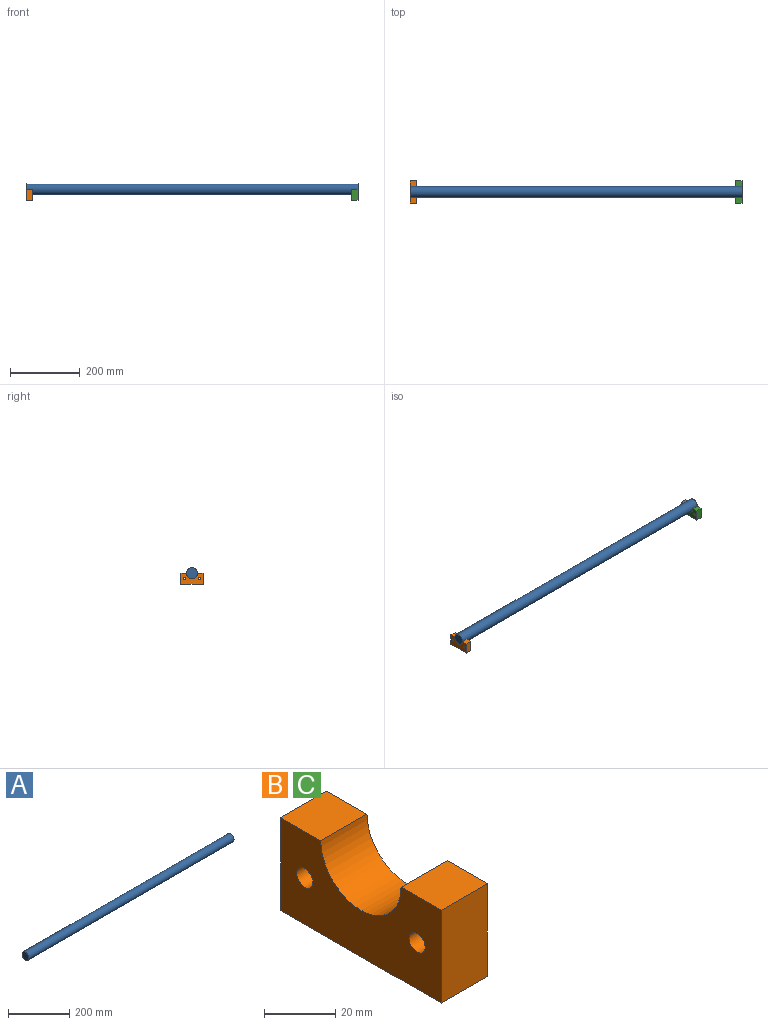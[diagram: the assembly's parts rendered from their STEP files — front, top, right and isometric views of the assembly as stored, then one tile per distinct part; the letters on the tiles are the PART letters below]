
ASSEMBLY  parts=3 mates=2
PART A: 3 faces, bbox 949.6x31.8x31.8 mm
  f0: cylinder r=15.88mm len=949.58mm, axis (1,0,0), area 94716.3mm2, adj f1,f2
  f1: plane 31.75x31.75mm, normal (-1,0,0), area 791.7mm2, adj f0
  f2: plane 31.75x31.75mm, normal (1,0,0), area 791.7mm2, adj f0
PART B: 10 faces, bbox 18.3x63.5x31.8 mm
  f0: plane 18.29x15.88mm, normal (0,0,1), area 290.3mm2, adj f1,f7,f8,f9
  f1: plane 31.75x18.29mm, normal (0,-1,0), area 580.6mm2, adj f0,f2,f8,f9
  f2: plane 63.5x18.29mm, normal (0,0,-1), area 1161.3mm2, adj f1,f3,f8,f9
  f3: plane 31.75x18.29mm, normal (0,1,0), area 580.6mm2, adj f2,f4,f8,f9
  f4: plane 18.29x15.88mm, normal (0,0,1), area 290.3mm2, adj f3,f7,f8,f9
  f5: cylinder r=3.17mm len=18.29mm, axis (-1,0,0), area 364.8mm2, adj f8,f9
  f6: cylinder r=3.17mm len=18.29mm, axis (-1,0,0), area 364.8mm2, adj f8,f9
  f7: cylinder r=15.88mm len=31.75mm, axis (-1,0,0), area 912.1mm2, adj f0,f4,f8,f9
  f8: plane 63.5x31.75mm, normal (1,0,0), area 1556.9mm2, adj f0,f1,f2,f3,f4,f5,f6,f7
  f9: plane 63.5x31.75mm, normal (-1,0,0), area 1556.9mm2, adj f0,f1,f2,f3,f4,f5,f6,f7
PART C: same geometry as B
PLACE A t=(484.01,-234.17,90.27)mm
PLACE B t=(-447.28,-234.17,90.27)mm
PLACE C t=(484.01,-234.17,90.27)mm fixed
MATE fastened C.f7 <-> A.f0  axis (1,0,0) through (493.16,-202.42,90.27)mm
MATE fastened C.f1 <-> B.f1  axis (0,-1,0) through (493.16,-234.17,58.52)mm
